# Revit family: Sanitary_Bath-screens_Modular system_Duscholux_SYSTEM210_S21-A
name_source: partatom
category: Aparatos sanitarios
units: mm (PartAtom-declared; Revit-internal decimal feet)

## family parameters
Compartido = No
Corte con vacíos al cargar = No
Cota de conector redondo = Diámetro de uso
Número OmniClass = 23.45.00.00
Punto de cálculo de habitación = No
Se basa en plano de trabajo = No
Siempre vertical = Sí
Tipo de pieza = Normal
Título OmniClass = Sanitary, Laundry, and Cleaning Equipment

## types (21) — shared parameters
Certified Quality UNE EN 14428 = http://www.duscholux.es
Combinations = Customizable upper guide
Components = Eropean components
Configuration enclosure = http://configuratumampara.duscholux.es
Código de montaje = C1030200
Descripción = Modular system with fixed segments + pivot doors at 180º for different types of rooms
Doors aperture = 650 mm  [stored 2.13255 ft]
Environmental Management ISO 14001 = ECOEMBES Certificate
Fabricante = Duscholux Ibérica, S.A.
Fact Sheet = https://duscholux.es
Glass Material = Glass_Material-Duscholux
Glass in Building UNE EN 12150 = CE Conformity marking
Handle Height = 1050 mm  [stored 3.44488 ft]
Height = 2500 mm  [stored 8.2021 ft]
IFC Classification = Furnishing Element
Image = https://duscholux.es
Lenght = 2800 mm  [stored 9.18635 ft]
Length Central fixed segments = 650 mm  [stored 2.13255 ft]
Length fixed segment 1 = 750 mm  [stored 2.46063 ft]
Length fixed segment 2 = 750 mm  [stored 2.46063 ft]
Maintenance and Cleaning = http://www.duscholux.es
Max Doors Height = 2100 mm
Max Height = 2500 mm  [stored 8.2021 ft]
Min Max Doors aperture = 650 mm  [stored 2.13255 ft]
Min Max Length = 2100 mm
Min Max Length Central fixed segments = 650 mm  [stored 2.13255 ft]
Min Max Length fixed segment = 750 mm  [stored 2.46063 ft]
Min Max Length fixed segment 2 = 750 mm  [stored 2.46063 ft]
NBS Reference Code = 45-35-70
NBS Reference Description = Shower Enclosures
Opening System = Pivot Door
Opening System Image = https://duscholux.es
Openning left angle = 0.00°
Openning right angle = 0.00°
Products = http://www.duscholux.es
Ref. = S21_A
Series = SYSTEM 210
Superior Glass Height = 366 mm
Technical Inspection Certificate (Applus) = http://www.duscholux.es
Thickness Fixed Segment = 8 mm  [stored 0.0262467 ft]
Thickness Glass = 6 mm  [stored 0.019685 ft]
UNSPSC Code = 30181507
URL = http://www.duscholux.es
Uniclass 2015 Code = PR-40-20-06-79
Uniclass 2015 Description = Shower Enclosures

## per-type parameters (varying)
| type | Accesories Material | Frame Material | Handle Material | Uper profile guide |
| Black Aluminium Finish | Anodized Aluminium_Duscholux Material-Black Finish | Anodized Aluminium_Duscholux Material-Black Finish | Anodized Aluminium_Duscholux Material-Black Finish | Anodized Aluminium_Duscholux Material-Black Finish |
| Black Aluminium Finish Superior guide Concrete PanElle | Anodized Aluminium_Duscholux Material-Black Finish | Anodized Aluminium_Duscholux Material-Black Finish | Anodized Aluminium_Duscholux Material-Black Finish | PanElle Concrete_Duscholux Material |
| Black Aluminium Finish Superior guide Basalt gray PanElle | Anodized Aluminium_Duscholux Material-Black Finish | Anodized Aluminium_Duscholux Material-Black Finish | Anodized Aluminium_Duscholux Material-Black Finish | PanElle Basalt Gray_Duscholux Material |
| Black Aluminium Finish Superior guide Metal gray PanElle | Anodized Aluminium_Duscholux Material-Black Finish | Anodized Aluminium_Duscholux Material-Black Finish | Anodized Aluminium_Duscholux Material-Black Finish | PanElle Metal Gray_Duscholux Material |
| Black Aluminium Finish Superior guide White PanElle | Anodized Aluminium_Duscholux Material-Black Finish | Anodized Aluminium_Duscholux Material-Black Finish | Anodized Aluminium_Duscholux Material-Black Finish | PanElle White_Duscholux Material |
| Black Aluminium Finish Superior guide Quartz PanElle | Anodized Aluminium_Duscholux Material-Black Finish | Anodized Aluminium_Duscholux Material-Black Finish | Anodized Aluminium_Duscholux Material-Black Finish | PanElle Quartz_DuscholuxMaterial |
| Black Aluminium Finish Superior guide Graphite PanElle | Anodized Aluminium_Duscholux Material-Black Finish | Anodized Aluminium_Duscholux Material-Black Finish | Anodized Aluminium_Duscholux Material-Black Finish | PanElle Graphite_DuscholuxMaterial |
| Platinum Aluminium Finish | Anodized Aluminium_Duscholux Material-Platinum Finish | Anodized Aluminium_Duscholux Material-Platinum Finish | Anodized Aluminium_Duscholux Material-Platinum Finish | Anodized Aluminium_Duscholux Material-Platinum Finish |
| Platinum Aluminium Finish Superior guide Basalt gray PanElle | Anodized Aluminium_Duscholux Material-Platinum Finish | Anodized Aluminium_Duscholux Material-Platinum Finish | Anodized Aluminium_Duscholux Material-Platinum Finish | PanElle Basalt Gray_Duscholux Material |
| Platinum Aluminium Finish Superior guide Metal gray PanElle | Anodized Aluminium_Duscholux Material-Platinum Finish | Anodized Aluminium_Duscholux Material-Platinum Finish | Anodized Aluminium_Duscholux Material-Platinum Finish | PanElle Metal Gray_Duscholux Material |
| Platinum Aluminium Finish Superior guide Concrete PanElle | Anodized Aluminium_Duscholux Material-Platinum Finish | Anodized Aluminium_Duscholux Material-Platinum Finish | Anodized Aluminium_Duscholux Material-Platinum Finish | PanElle Concrete_Duscholux Material |
| Platinum Aluminium Finish Superior guide Graphite PanElle | Anodized Aluminium_Duscholux Material-Platinum Finish | Anodized Aluminium_Duscholux Material-Platinum Finish | Anodized Aluminium_Duscholux Material-Platinum Finish | PanElle Graphite_DuscholuxMaterial |
| Platinum Aluminium Finish Superior guide Quartz PanElle | Anodized Aluminium_Duscholux Material-Platinum Finish | Anodized Aluminium_Duscholux Material-Platinum Finish | Anodized Aluminium_Duscholux Material-Platinum Finish | PanElle Quartz_DuscholuxMaterial |
| Platinum Aluminium Finish Superior guide White PanElle | Anodized Aluminium_Duscholux Material-Platinum Finish | Anodized Aluminium_Duscholux Material-Platinum Finish | Anodized Aluminium_Duscholux Material-Platinum Finish | PanElle White_Duscholux Material |
| Matte Silver Aluminium Finish | Anodized Aluminium_Duscholux Material-Matte Silver Finish | Anodized Aluminium_Duscholux Material-Matte Silver Finish | Anodized Aluminium_Duscholux Material-Matte Silver Finish | Anodized Aluminium_Duscholux Material-Matte Silver Finish |
| Matte Silver Aluminium Finish Superior guide Basalt gray PanElle | Anodized Aluminium_Duscholux Material-Matte Silver Finish | Anodized Aluminium_Duscholux Material-Matte Silver Finish | Anodized Aluminium_Duscholux Material-Matte Silver Finish | PanElle Basalt Gray_Duscholux Material |
| Matte Silver Aluminium Finish Superior guide Metal gray PanElle | Anodized Aluminium_Duscholux Material-Matte Silver Finish | Anodized Aluminium_Duscholux Material-Matte Silver Finish | Anodized Aluminium_Duscholux Material-Matte Silver Finish | PanElle Metal Gray_Duscholux Material |
| Matte Silver Aluminium Finish Superior guide Concrete PanElle | Anodized Aluminium_Duscholux Material-Matte Silver Finish | Anodized Aluminium_Duscholux Material-Matte Silver Finish | Anodized Aluminium_Duscholux Material-Matte Silver Finish | PanElle Concrete_Duscholux Material |
| Matte Silver Aluminium Finish Superior guide Graphite PanElle | Anodized Aluminium_Duscholux Material-Matte Silver Finish | Anodized Aluminium_Duscholux Material-Matte Silver Finish | Anodized Aluminium_Duscholux Material-Matte Silver Finish | PanElle Graphite_DuscholuxMaterial |
| Matte Silver Aluminium Finish Superior guide Quartz PanElle | Anodized Aluminium_Duscholux Material-Matte Silver Finish | Anodized Aluminium_Duscholux Material-Matte Silver Finish | Anodized Aluminium_Duscholux Material-Matte Silver Finish | PanElle Quartz_DuscholuxMaterial |
| Matte Silver Aluminium Finish Superior guide White PanElle | Anodized Aluminium_Duscholux Material-Matte Silver Finish | Anodized Aluminium_Duscholux Material-Matte Silver Finish | Anodized Aluminium_Duscholux Material-Matte Silver Finish | PanElle White_Duscholux Material |

note: [stored X ft] marks values corroborated as IEEE doubles in the binary element streams (Revit-internal decimal feet)
